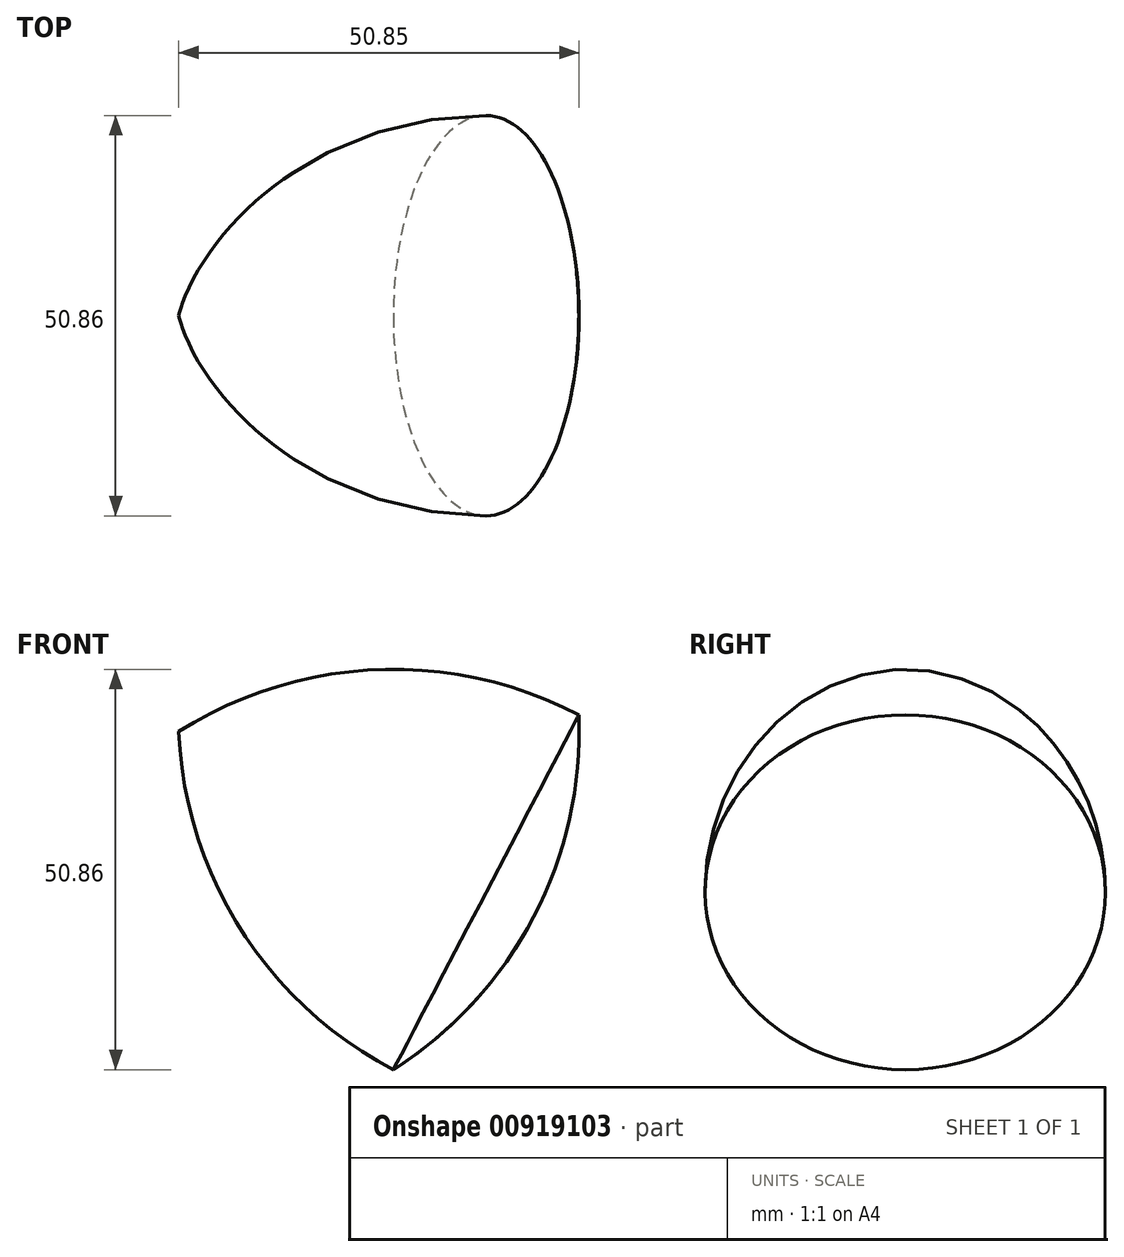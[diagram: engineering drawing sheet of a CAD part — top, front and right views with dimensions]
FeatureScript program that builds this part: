
annotation { "Feature Type Name" : "Feature", "Feature Type Description" : "" }
export const myFeature = defineFeature(function(context is Context, id is Id, definition is map)
    precondition{}
    {
        {
            var Q0;
            Q0=qCreatedBy(makeId("Front.planeOp"),FACE);
            var sketch = newSketch(context, id + "F0", { "sketchPlane" : qUnion([Q0])});
            skCircle(sketch, "E0.cCircle", {"center": v(0, 0) * mm, "radius": 14.68 * mm, "construction": true});
            skLineSegment(sketch, "E0.0", {"start": v(-26.02, 13.6) * mm, "end": v(24.79, 15.74) * mm});
            skLineSegment(sketch, "E0.1", {"start": v(24.79, 15.74) * mm, "end": v(1.24, -29.34) * mm});
            skLineSegment(sketch, "E0.2", {"start": v(1.24, -29.34) * mm, "end": v(-26.02, 13.6) * mm});
            skPoint(sketch, "E0.0.midPoint", {"position": v(-0.62, 14.67) * mm});
            skArc(sketch, "E1", {"start": v(1.24, -29.34) * mm, "mid": v(19.05, -9.95) * mm, "end": v(24.79, 15.74) * mm});
            skArc(sketch, "E2", {"start": v(-26.02, 13.6) * mm, "mid": v(-18.15, -11.52) * mm, "end": v(1.24, -29.34) * mm});
            skArc(sketch, "E3", {"start": v(24.79, 15.74) * mm, "mid": v(-0.9, 21.48) * mm, "end": v(-26.02, 13.6) * mm});
            skLineSegment(sketch, "E4", {"start": v(-26.02, 13.6) * mm, "end": v(19.05, -9.95) * mm});
            skPoint(sketch, "E5", {"position": v(-20.26, -7.87) * mm});
            skPoint(sketch, "E5.positionSnap0", {"position": v(-12.4, -7.87) * mm});
            skPoint(sketch, "E6", {"position": v(-0.9, 21.48) * mm});
            skSolve(sketch);
        }
        {
            var Q0;
            Q0=makeQuery(id+"F0.imprint","IMPRINT",FACE,{"disambiguationData":[TD([[makeQuery(id+"F0.imprint","IMPRINT",EDGE,{"derivedFrom":sQuery(id+"F0.wireOp",EDGE,"E0.2")}),1.0]])]});
            var Q1;
            {var subQ1=sQuery(id+"F0.wireOp",EDGE,"E0.2");Q1=makeQuery(id+"F0.imprint","IMPRINT",FACE,{"disambiguationData":[TD([[makeQuery(id+"F0.imprint","IMPRINT",EDGE,{"derivedFrom":subQ1}),-1.0]])]});}
            var Q2;
            {var subQ0=sQuery(id+"F0.wireOp",EDGE,"E1");var subQ3=sQuery(id+"F0.wireOp",EDGE,"E4");var subQ5=makeQuery(id+"F0.imprint","INTERSECT",VERTEX,{"derivedFrom":[subQ0,subQ3]});Q2=makeQuery(id+"F0.imprint","IMPRINT",FACE,{"disambiguationData":[TD([[makeQuery(id+"F0.imprint","IMPRINT",EDGE,{"disambiguationData":[TD([[subQ5,1.0]])],"derivedFrom":subQ3}),-1.0]])]});}
            var Q3;
            Q3=sQuery(id+"F0.wireOp",EDGE,"E4");
            revolve(context, id + "F1", {"surfaceOperationType" : NewSurfaceOperationType.NEW, "entities" : qUnion([Q0, Q1, Q2]), "axis" : qUnion([Q3]), "revolveType" : RevolveType.FULL});
        }
    });
